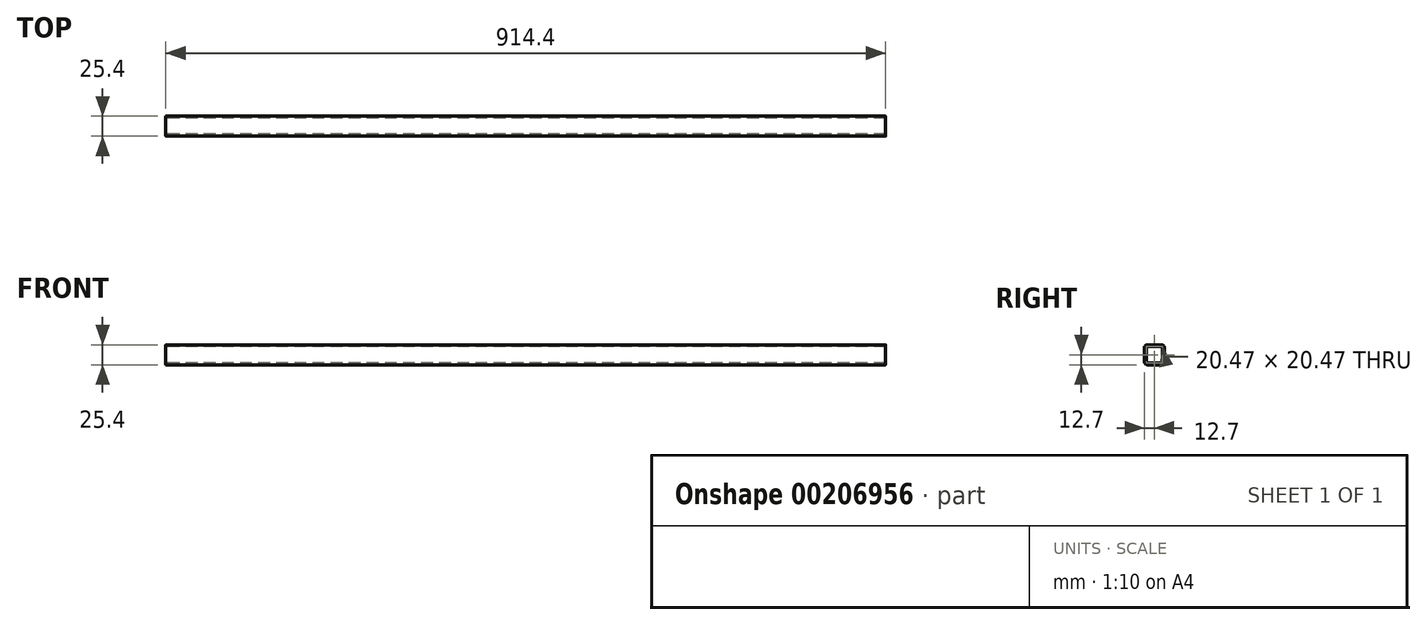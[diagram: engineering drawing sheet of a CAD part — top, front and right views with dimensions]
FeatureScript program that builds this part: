
annotation { "Feature Type Name" : "Feature", "Feature Type Description" : "" }
export const myFeature = defineFeature(function(context is Context, id is Id, definition is map)
    precondition{}
    {
        {
            var Q0;
            Q0=qCreatedBy(makeId("Right.planeOp"),FACE);
            var sketch = newSketch(context, id + "F0", { "sketchPlane" : qUnion([Q0])});
            skLineSegment(sketch, "E0.bottom", {"start": v(3.8, 0) * mm, "end": v(21.59, 0) * mm});
            skLineSegment(sketch, "E0.top", {"start": v(3.8, 25.4) * mm, "end": v(21.59, 25.4) * mm});
            skLineSegment(sketch, "E0.left", {"start": v(0, 3.81) * mm, "end": v(0, 21.6) * mm});
            skLineSegment(sketch, "E0.right", {"start": v(25.4, 3.81) * mm, "end": v(25.4, 21.6) * mm});
            skPoint(sketch, "E1.visualSharp", {"position": v(25.4, 0) * mm});
            skArc(sketch, "E1.filletArc", {"start": v(21.59, 0) * mm, "mid": v(24.28, 1.12) * mm, "end": v(25.4, 3.81) * mm});
            skPoint(sketch, "E2.visualSharp", {"position": v(0, 0) * mm});
            skArc(sketch, "E2.filletArc", {"start": v(0, 3.8) * mm, "mid": v(1.12, 1.12) * mm, "end": v(3.8, 0) * mm});
            skPoint(sketch, "E3.visualSharp", {"position": v(0, 25.4) * mm});
            skArc(sketch, "E3.filletArc", {"start": v(3.8, 25.4) * mm, "mid": v(1.12, 24.28) * mm, "end": v(0, 21.6) * mm});
            skPoint(sketch, "E4.visualSharp", {"position": v(25.4, 25.4) * mm});
            skArc(sketch, "E4.filletArc", {"start": v(25.4, 21.6) * mm, "mid": v(24.28, 24.28) * mm, "end": v(21.59, 25.4) * mm});
            skLineSegment(sketch, "E5.bottom", {"start": v(2.46, 22.94) * mm, "end": v(22.94, 22.94) * mm});
            skLineSegment(sketch, "E5.top", {"start": v(2.46, 2.46) * mm, "end": v(22.94, 2.46) * mm});
            skLineSegment(sketch, "E5.left", {"start": v(2.46, 22.94) * mm, "end": v(2.46, 2.46) * mm});
            skLineSegment(sketch, "E5.right", {"start": v(22.94, 22.94) * mm, "end": v(22.94, 2.46) * mm});
            skLineSegment(sketch, "E6", {"start": v(1.12, 24.28) * mm, "end": v(3.81, 21.59) * mm, "construction": true});
            skPoint(sketch, "E7", {"position": v(2.46, 22.94) * mm});
            skLineSegment(sketch, "E8", {"start": v(24.28, 1.12) * mm, "end": v(21.59, 3.81) * mm, "construction": true});
            skPoint(sketch, "E9", {"position": v(22.94, 2.46) * mm});
            skSolve(sketch);
        }
        {
            var Q0;
            Q0=makeQuery(id+"F0.imprint","IMPRINT",FACE,{"disambiguationData":[TD([[makeQuery(id+"F0.imprint","IMPRINT",EDGE,{"derivedFrom":sQuery(id+"F0.wireOp",EDGE,"E0.bottom")}),1.0]])]});
            extrude(context, id + "F1", {"entities" : qUnion([Q0]), "depth" : 914.4 * mm});
        }
    });
